# Revit family: WT14-2
name_source: partatom
category: Lighting Fixtures
revit_build: Autodesk Revit Architecture 2012 (Build: 20110309_2315(x64)
units: mm (PartAtom-declared; Revit-internal decimal feet)

## types (4) — shared parameters
Color Filter = 16777215
Default Elevation = 48"
Description = Wet Location Lensed Troffer.
Dimming Lamp Color Temperature Shift = <None>
Emit from Line Length = 24"
Finish = White
Finish2 = White
Lamp = F32T8
Length = 48"
Manufacturer = Columbia Lighting
Manufacturer Fax = (866)-898-1065
Model = WT14-2
Opal lens = Etched Glass
Product Documentation Link = http://www.columbialighting.com
Product Page URL = http://www.columbialighting.com
Tilt Angle = -90.00°
URL = http://www.columbialighting.com
Wattage Comments = 32 W
Width = 12"

## per-type parameters (varying)
| type | Photometric Web File |
| WT14-132G-FSA12-E-PAF | 13751.IES |
| WT14-232G-FSA12-E | 13533.IES |
| WT14-232G-FSA12-E-PAF | 13763.IES |
| WT14-332G-FSA12-E-PAF | 13752.IES |

## geometry (parser evidence)
native form markers: Sweep x3
no freeform markers — native parametric forms only
